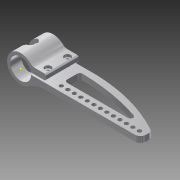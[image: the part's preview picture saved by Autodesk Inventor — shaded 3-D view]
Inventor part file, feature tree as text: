
AUTODESK INVENTOR PART (.ipt)
format: ipt  version: 2015 (Build 190159000, 159)  size: 214,016 bytes
history: native  units: mm
features: sketch x5, extrude x3, fillet x3, hole x2
ambient origin geometry x8: Origin, YZ Plane, XZ Plane, XY Plane, X Axis, Y Axis, Z Axis, Center Point
bodies: Solid1 (feature_tree)
feature tree (13):
  extrude  "Extrusion1"  Depth=42.0mm
  hole  "Hole1"  [1 undecoded]
  hole  "Hole2"  [1 undecoded]
  sketch  "Sketch3"  dims[d2=168.0mm d3=9.0mm]
  fillet  "Fillet1"  Radius=39.0mm
  sketch  "Sketch4"  dims[d4=50.0mm d7=3.0mm d8=39.0mm]
  extrude  "Extrusion3"  Depth=3.0mm
  extrude  "Extrusion5"  Depth=10.0mm
  fillet  "Fillet2"  Radius=50.0mm
  fillet  "Fillet3"  Radius=2.5mm
  sketch  "Sketch1"  dims[d0=32.0mm d1=42.0mm]
  sketch  "Sketch5"  dims[d9=9.0mm d10=3.0mm]
  sketch  "Sketch9"  dims[d11=39.0mm d12=10.0mm d13=50.0mm d14=0.0mm d15=10.0mm d16=7.0mm d17=5.5mm d18=6.0mm d19=10.0mm d20=4.0mm d21=90.0deg d22=8.0mm d23=20.594885mm d24=10.0mm d25=7.0mm d26=5.5mm d27=6.0mm d28=10.0mm d29=4.0mm d30=90.0deg d31=8.0mm d32=20.594885mm d40=2.5mm d41=17.0mm d42=40.0mm d43=16.0mm d44=40.0mm d45=8.0mm d46=10.0mm d47=0.0mm d65=10.0mm d66=0.0mm d67=4.0mm d68=8.0mm]
note: 2 required parameter values undecoded (feature->parameter linkage not recoverable at this tier; creation-order binding heuristic only, values carry confidence <= 0.55)
